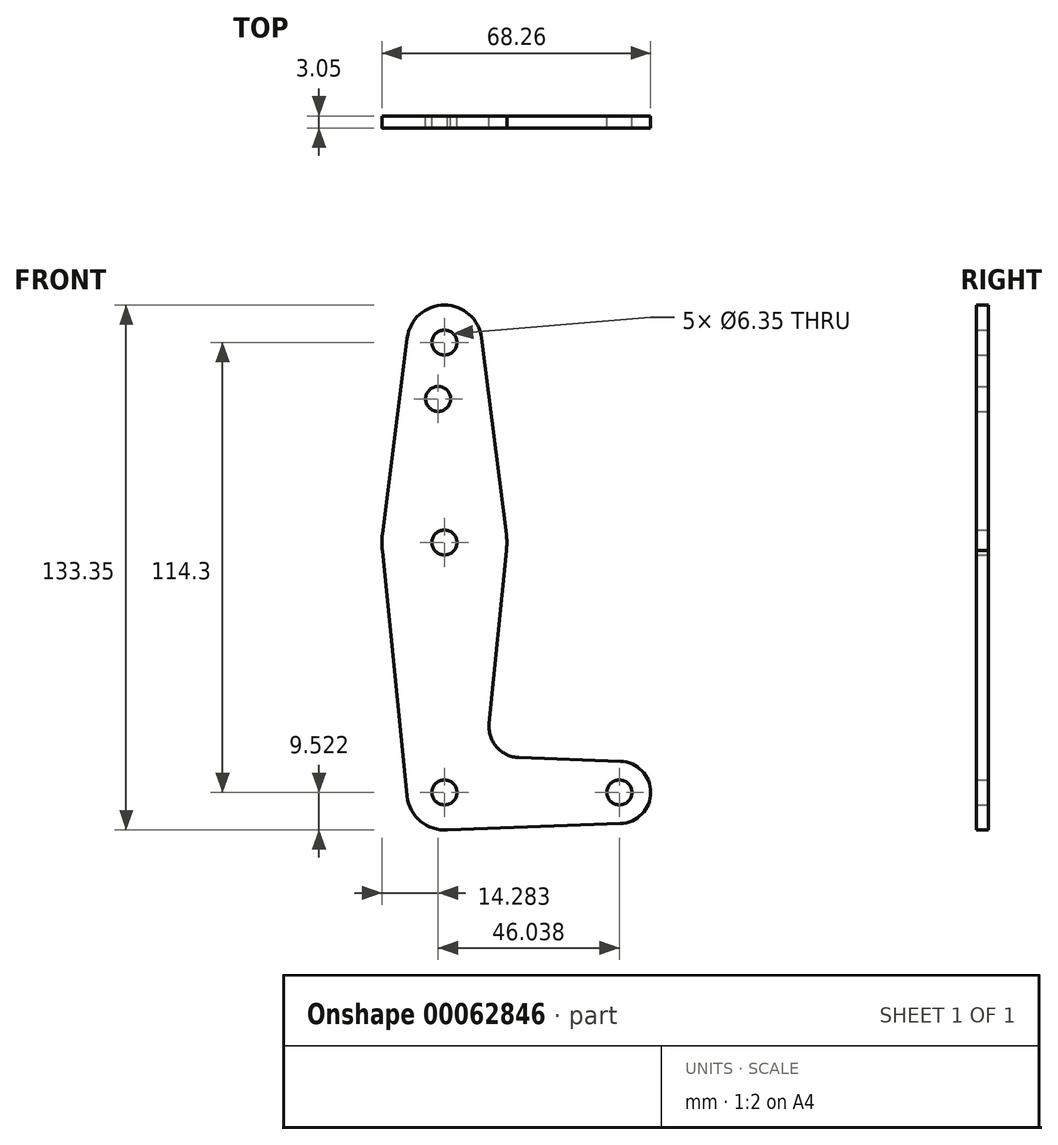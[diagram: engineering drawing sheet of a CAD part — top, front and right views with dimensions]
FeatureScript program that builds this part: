
annotation { "Feature Type Name" : "Feature", "Feature Type Description" : "" }
export const myFeature = defineFeature(function(context is Context, id is Id, definition is map)
    precondition{}
    {
        {
            var Q0;
            Q0=qCreatedBy(makeId("Front.planeOp"),FACE);
            var sketch = newSketch(context, id + "F0", { "sketchPlane" : qUnion([Q0])});
            skLineSegment(sketch, "E0", {"start": v(-14.84, -8.39) * mm, "end": v(29.61, -8.39) * mm, "construction": true});
            skCircle(sketch, "E1", {"center": v(-14.84, 105.91) * mm, "radius": 9.53 * mm});
            skCircle(sketch, "E2", {"center": v(-14.84, -8.39) * mm, "radius": 9.53 * mm});
            skCircle(sketch, "E3", {"center": v(29.61, -8.39) * mm, "radius": 7.94 * mm});
            skCircle(sketch, "E4", {"center": v(-14.84, 55.11) * mm, "radius": 15.88 * mm});
            skLineSegment(sketch, "E5", {"start": v(-24.29, 107.1) * mm, "end": v(-30.59, 57.1) * mm});
            skLineSegment(sketch, "E6", {"start": v(-5.39, 107.1) * mm, "end": v(0.91, 57.1) * mm});
            skLineSegment(sketch, "E7", {"start": v(-14.84, 105.91) * mm, "end": v(-14.84, -8.39) * mm, "construction": true});
            skLineSegment(sketch, "E8", {"start": v(-30.59, 53.13) * mm, "end": v(-24.32, -9.34) * mm});
            skLineSegment(sketch, "E9", {"start": v(0.91, 53.13) * mm, "end": v(-3.5, 9.2) * mm});
            skLineSegment(sketch, "E10", {"start": v(-15.01, -17.91) * mm, "end": v(29.9, -16.32) * mm});
            skLineSegment(sketch, "E11", {"start": v(4.13, 0.46) * mm, "end": v(29.9, -0.46) * mm});
            skCircle(sketch, "E12", {"center": v(-14.84, 105.91) * mm, "radius": 3.18 * mm});
            skCircle(sketch, "E13", {"center": v(-14.84, 55.11) * mm, "radius": 3.18 * mm});
            skCircle(sketch, "E14", {"center": v(-14.84, -8.39) * mm, "radius": 3.18 * mm});
            skCircle(sketch, "E15", {"center": v(29.61, -8.39) * mm, "radius": 3.18 * mm});
            skCircle(sketch, "E16", {"center": v(-16.43, 91.6) * mm, "radius": 3.18 * mm});
            skArc(sketch, "E17.filletArc", {"start": v(-3.5, 9.2) * mm, "mid": v(-1.58, 3.18) * mm, "end": v(4.13, 0.46) * mm});
            skSolve(sketch);
        }
        {
            var Q0;
            Q0 = qSketchRegion(id + "F0", true);
            extrude(context, id + "F1", {"entities" : qUnion([Q0]), "depth" : 3.05 * mm});
        }
    });
